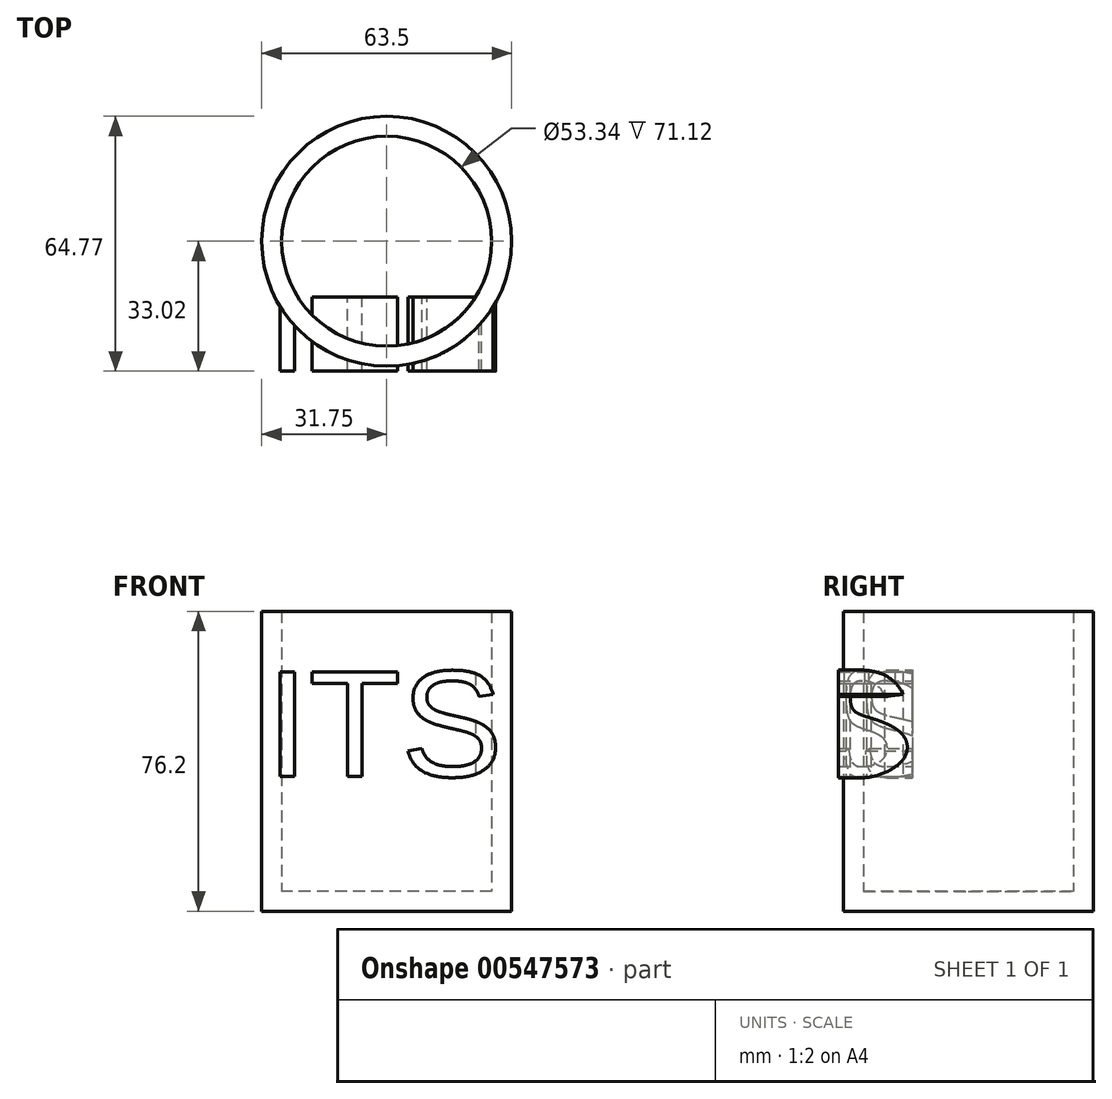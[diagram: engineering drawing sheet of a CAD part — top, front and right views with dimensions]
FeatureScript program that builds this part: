
annotation { "Feature Type Name" : "Feature", "Feature Type Description" : "" }
export const myFeature = defineFeature(function(context is Context, id is Id, definition is map)
    precondition{}
    {
        {
            var Q0;
            Q0=qCreatedBy(makeId("Top.planeOp"),FACE);
            var sketch = newSketch(context, id + "F0", { "sketchPlane" : qUnion([Q0])});
            skCircle(sketch, "E0", {"center": v(0, 0) * mm, "radius": 31.75 * mm});
            skSolve(sketch);
        }
        {
            var Q0;
            Q0=makeQuery(id+"F0.imprint","IMPRINT",FACE,{"disambiguationData":[TD([[makeQuery(id+"F0.imprint","IMPRINT",EDGE,{"derivedFrom":sQuery(id+"F0.wireOp",EDGE,"E0")}),1.0]])]});
            extrude(context, id + "F1", {"entities" : qUnion([Q0]), "depth" : 76.2 * mm, "offsetDistance" : 25.4 * mm});
        }
        {
            var Q0;
            Q0=makeQuery(id+"F1.opExtrude","CAP_FACE",FACE,{"disambiguationData":[OSD([sQuery(id+"F0.wireOp",EDGE,"E0")])],"isStart":false});
            shell(context, id + "F2", {"entities" : qUnion([Q0]), "thickness" : 5.08 * mm});
        }
        {
            var Q0;
            Q0=qCreatedBy(makeId("Front.planeOp"),FACE);
            cPlane(context, id + "F3", {"entities" : qUnion([Q0]), "cplaneType" : CPlaneType.OFFSET, "offset" : 14.22 * mm, "width" : 152.4 * mm, "height" : 152.4 * mm});
        }
        {
            var Q0;
            Q0=qCreatedBy(id+"F3.planeOp",FACE);
            var sketch = newSketch(context, id + "F4", { "sketchPlane" : qUnion([Q0])});
            skText(sketch, "E1", { "text": "ITS", "fontName": "Arimo-Regular.ttf"});
            const initialGuessF4  = {"E1": [-0.03059, 0.0343, 1, 0, 0.02778]};
            skSetInitialGuess(sketch, initialGuessF4);
            skSolve(sketch);
        }
        {
            var Q0;
            Q0 = qSketchRegion(id + "F4", true);
            extrude(context, id + "F5", {"entities" : qUnion([Q0]), "operationType" : NewBodyOperationType.ADD, "depth" : 18.8 * mm, "offsetDistance" : 25.4 * mm});
        }
    });
